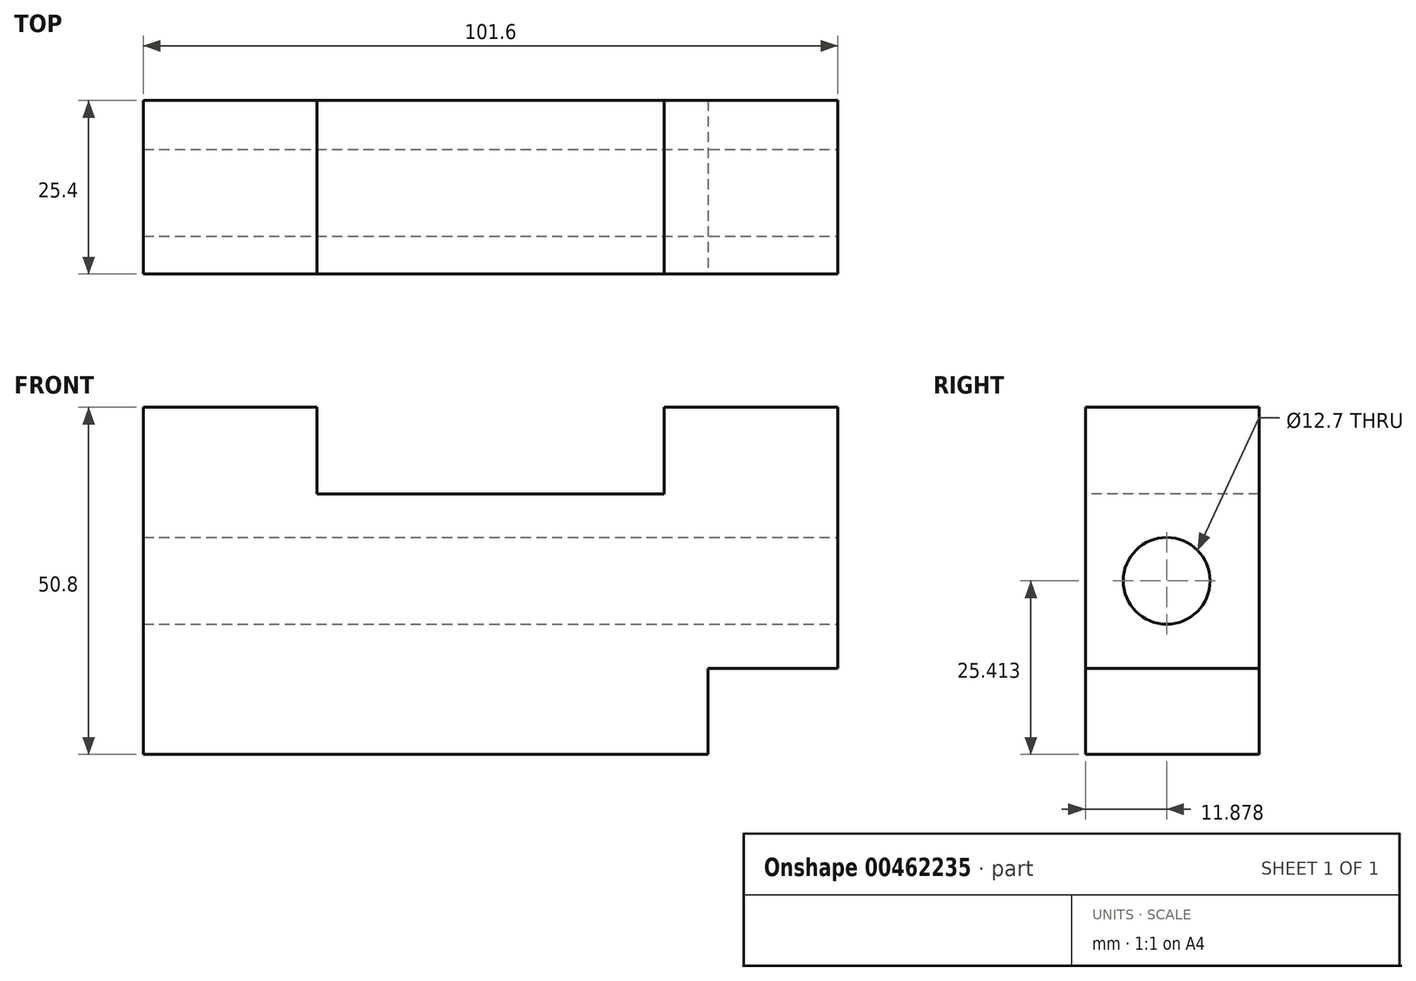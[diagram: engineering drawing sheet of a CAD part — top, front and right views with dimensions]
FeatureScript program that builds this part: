
annotation { "Feature Type Name" : "Feature", "Feature Type Description" : "" }
export const myFeature = defineFeature(function(context is Context, id is Id, definition is map)
    precondition{}
    {
        {
            var Q0;
            Q0=qCreatedBy(makeId("Front.planeOp"),FACE);
            var sketch = newSketch(context, id + "F0", { "sketchPlane" : qUnion([Q0])});
            skLineSegment(sketch, "E0.bottom", {"start": v(50.8, 25.4) * mm, "end": v(-50.8, 25.4) * mm});
            skLineSegment(sketch, "E0.top", {"start": v(50.8, -25.4) * mm, "end": v(-50.8, -25.4) * mm});
            skLineSegment(sketch, "E0.left", {"start": v(50.8, 25.4) * mm, "end": v(50.8, -25.4) * mm});
            skLineSegment(sketch, "E0.right", {"start": v(-50.8, 25.4) * mm, "end": v(-50.8, -25.4) * mm});
            skPoint(sketch, "E0.middle", {"position": v(0, 0) * mm});
            skSolve(sketch);
        }
        {
            var Q0;
            Q0 = qSketchRegion(id + "F0", true);
            extrude(context, id + "F1", {"entities" : qUnion([Q0]), "depth" : 25.4 * mm});
        }
        {
            var Q0;
            Q0=makeQuery(id+"F1.opExtrude","CAP_FACE",FACE,{"disambiguationData":[OSD([sQuery(id+"F0.wireOp",EDGE,"E0.bottom"),sQuery(id+"F0.wireOp",EDGE,"E0.top"),sQuery(id+"F0.wireOp",EDGE,"E0.left"),sQuery(id+"F0.wireOp",EDGE,"E0.right")])],"isStart":false});
            var sketch = newSketch(context, id + "F2", { "sketchPlane" : qUnion([Q0])});
            skLineSegment(sketch, "E1.bottom", {"start": v(-25.4, 25.4) * mm, "end": v(25.4, 25.4) * mm});
            skLineSegment(sketch, "E1.top", {"start": v(-25.4, 12.7) * mm, "end": v(25.4, 12.7) * mm});
            skLineSegment(sketch, "E1.left", {"start": v(-25.4, 25.4) * mm, "end": v(-25.4, 12.7) * mm});
            skLineSegment(sketch, "E1.right", {"start": v(25.4, 25.4) * mm, "end": v(25.4, 12.7) * mm});
            skSolve(sketch);
        }
        {
            var Q0;
            Q0 = qSketchRegion(id + "F2", true);
            extrude(context, id + "F3", {"entities" : qUnion([Q0]), "operationType" : NewBodyOperationType.REMOVE, "endBound" : BoundingType.THROUGH_ALL, "oppositeDirection" : true, "depth" : 25.4 * mm});
        }
        {
            var Q0;
            Q0=qCreatedBy(makeId("Front.planeOp"),FACE);
            var sketch = newSketch(context, id + "F4", { "sketchPlane" : qUnion([Q0])});
            skLineSegment(sketch, "E2.bottom", {"start": v(50.88, -12.8) * mm, "end": v(31.83, -12.8) * mm});
            skLineSegment(sketch, "E2.top", {"start": v(50.88, -25.5) * mm, "end": v(31.83, -25.5) * mm});
            skLineSegment(sketch, "E2.left", {"start": v(50.88, -12.8) * mm, "end": v(50.88, -25.5) * mm});
            skLineSegment(sketch, "E2.right", {"start": v(31.83, -12.8) * mm, "end": v(31.83, -25.5) * mm});
            skSolve(sketch);
        }
        {
            var Q0;
            Q0 = qSketchRegion(id + "F4", true);
            extrude(context, id + "F5", {"entities" : qUnion([Q0]), "operationType" : NewBodyOperationType.REMOVE, "endBound" : BoundingType.THROUGH_ALL, "depth" : 25.4 * mm});
        }
        {
            var Q0;
            Q0=qCreatedBy(makeId("Right.planeOp"),FACE);
            var sketch = newSketch(context, id + "F6", { "sketchPlane" : qUnion([Q0])});
            skCircle(sketch, "E3", {"center": v(-13.52, 0.01) * mm, "radius": 6.35 * mm});
            skSolve(sketch);
        }
        {
            var Q0;
            Q0 = qSketchRegion(id + "F6", true);
            extrude(context, id + "F7", {"entities" : qUnion([Q0]), "operationType" : NewBodyOperationType.REMOVE, "endBound" : BoundingType.THROUGH_ALL, "oppositeDirection" : true, "depth" : 25.4 * mm});
        }
        {
            var Q0;
            Q0 = qSketchRegion(id + "F6", true);
            extrude(context, id + "F8", {"entities" : qUnion([Q0]), "operationType" : NewBodyOperationType.REMOVE, "endBound" : BoundingType.THROUGH_ALL, "depth" : 25.4 * mm});
        }
    });
